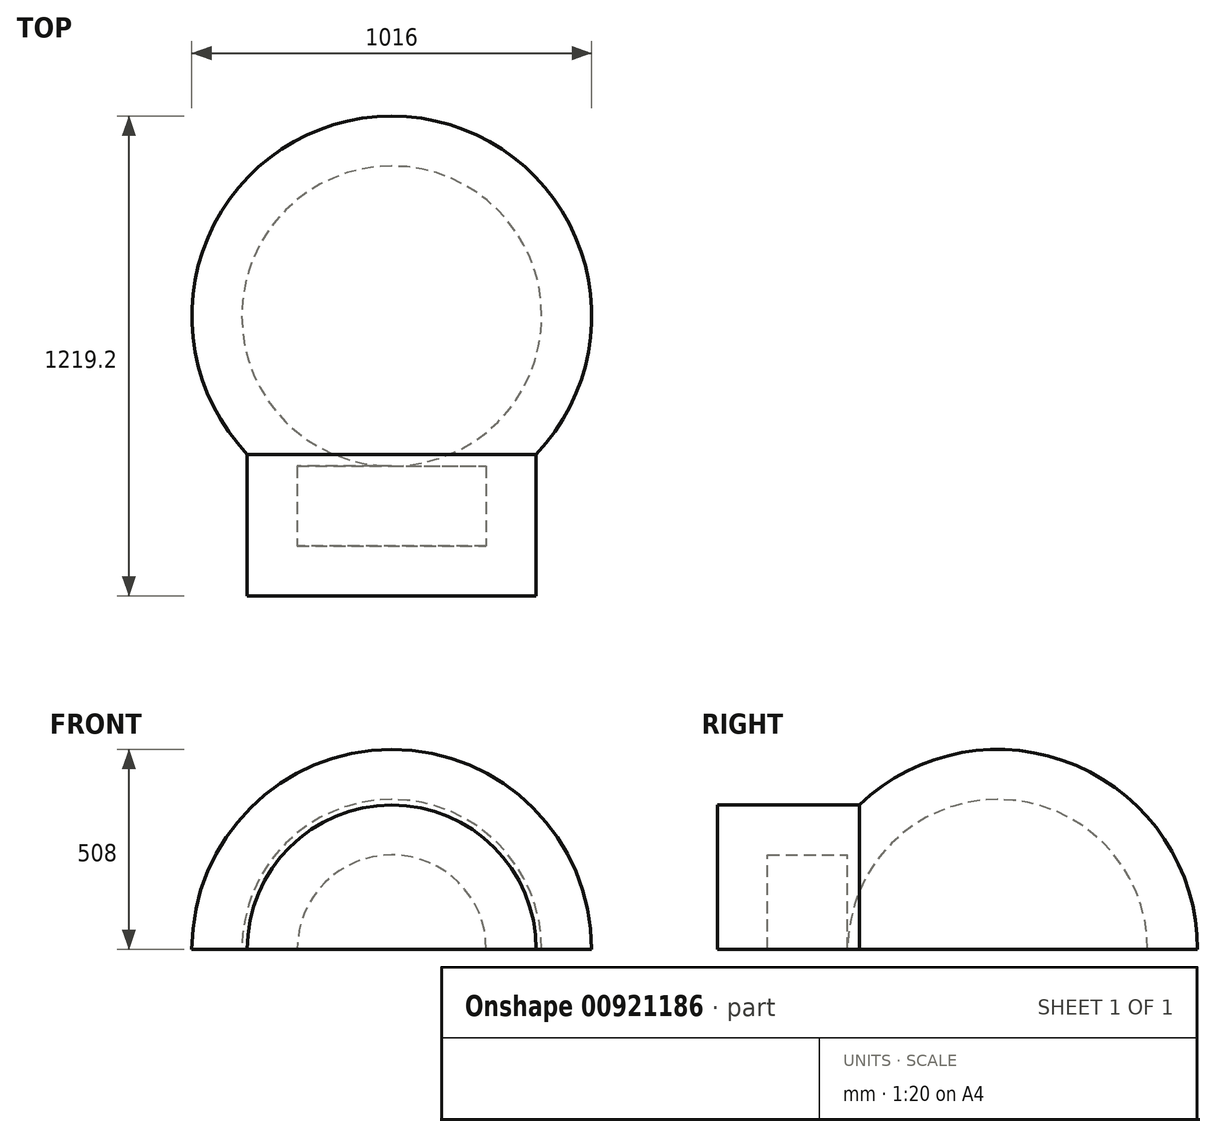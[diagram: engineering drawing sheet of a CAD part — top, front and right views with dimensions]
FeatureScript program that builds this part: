
annotation { "Feature Type Name" : "Feature", "Feature Type Description" : "" }
export const myFeature = defineFeature(function(context is Context, id is Id, definition is map)
    precondition{}
    {
        {
            var Q0;
            Q0=qCreatedBy(makeId("Top.planeOp"),FACE);
            var sketch = newSketch(context, id + "F0", { "sketchPlane" : qUnion([Q0])});
            skArc(sketch, "E0", {"start": v(0, -381) * mm, "mid": v(381, 0) * mm, "end": v(0, 381) * mm});
            skLineSegment(sketch, "E1", {"start": v(0, 381) * mm, "end": v(0, -381) * mm});
            skLineSegment(sketch, "E2.bottom", {"start": v(0, -381) * mm, "end": v(240.03, -381) * mm});
            skLineSegment(sketch, "E2.top", {"start": v(0, -584.2) * mm, "end": v(240.03, -584.2) * mm});
            skLineSegment(sketch, "E2.left", {"start": v(0, -381) * mm, "end": v(0, -584.2) * mm});
            skLineSegment(sketch, "E2.right", {"start": v(240.03, -381) * mm, "end": v(240.03, -584.2) * mm});
            skArc(sketch, "E3.0", {"start": v(367.03, -351.22) * mm, "mid": v(467.16, 199.56) * mm, "end": v(0, 508) * mm});
            skLineSegment(sketch, "E3.1", {"start": v(367.03, -351.22) * mm, "end": v(367.03, -711.2) * mm});
            skLineSegment(sketch, "E3.2", {"start": v(0, -711.2) * mm, "end": v(367.03, -711.2) * mm});
            skLineSegment(sketch, "E4", {"start": v(0, -711.2) * mm, "end": v(0, -584.2) * mm});
            skLineSegment(sketch, "E5", {"start": v(0, 381) * mm, "end": v(0, 508) * mm});
            skSolve(sketch);
        }
        {
            var Q0;
            Q0=makeQuery(id+"F0.imprint","IMPRINT",FACE,{"disambiguationData":[TD([[makeQuery(id+"F0.imprint","IMPRINT",EDGE,{"derivedFrom":sQuery(id+"F0.wireOp",EDGE,"E0")}),-1.0]])]});
            var Q1;
            Q1=sQuery(id+"F0.wireOp",EDGE,"E1");
            revolve(context, id + "F1", {"surfaceOperationType" : NewSurfaceOperationType.NEW, "entities" : qUnion([Q0]), "axis" : qUnion([Q1]), "revolveType" : RevolveType.ONE_DIRECTION, "angle" : 180 * degree});
        }
    });
